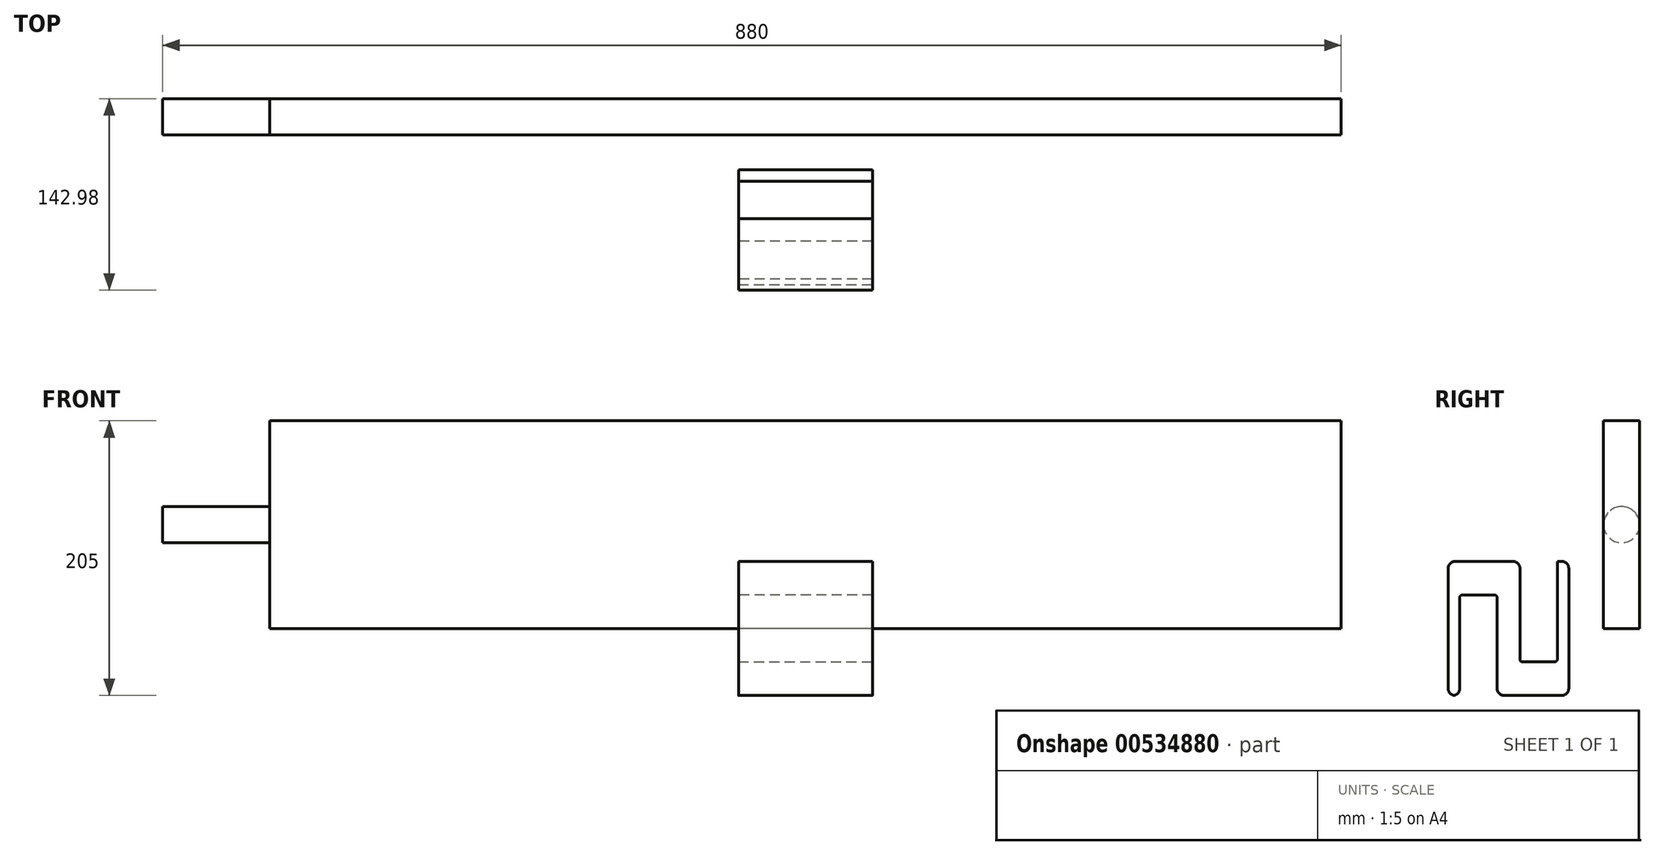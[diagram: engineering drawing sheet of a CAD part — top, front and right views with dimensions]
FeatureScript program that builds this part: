
annotation { "Feature Type Name" : "Feature", "Feature Type Description" : "" }
export const myFeature = defineFeature(function(context is Context, id is Id, definition is map)
    precondition{}
    {
        {
            var Q0;
            Q0=qCreatedBy(makeId("Front.planeOp"),FACE);
            var sketch = newSketch(context, id + "F0", { "sketchPlane" : qUnion([Q0])});
            skLineSegment(sketch, "E0.bottom", {"start": v(50, 50) * mm, "end": v(-50, 50) * mm});
            skLineSegment(sketch, "E0.top", {"start": v(50, -50) * mm, "end": v(-50, -50) * mm});
            skLineSegment(sketch, "E0.left", {"start": v(50, 50) * mm, "end": v(50, -50) * mm});
            skLineSegment(sketch, "E0.right", {"start": v(-50, 50) * mm, "end": v(-50, -50) * mm});
            skPoint(sketch, "E0.middle", {"position": v(0, 0) * mm});
            skSolve(sketch);
        }
        {
            var Q0;
            Q0 = qSketchRegion(id + "F0", true);
            extrude(context, id + "F1", {"entities" : qUnion([Q0]), "endBound" : BoundingType.SYMMETRIC, "depth" : 45 * mm, "offsetDistance" : 25 * mm});
        }
        {
            var Q0;
            Q0=makeQuery(id+"F1.opExtrude","SWEPT_FACE",FACE,{"disambiguationData":[OSD([sQuery(id+"F0.wireOp",EDGE,"E0.left")])]});
            var sketch = newSketch(context, id + "F2", { "sketchPlane" : qUnion([Q0])});
            skLineSegment(sketch, "E1.bottom", {"start": v(-14, 50) * mm, "end": v(14, 50) * mm});
            skLineSegment(sketch, "E1.top", {"start": v(-14, -25) * mm, "end": v(14, -25) * mm});
            skLineSegment(sketch, "E1.left", {"start": v(-14, 50) * mm, "end": v(-14, -25) * mm});
            skLineSegment(sketch, "E1.right", {"start": v(14, 50) * mm, "end": v(14, -25) * mm});
            skLineSegment(sketch, "E2.bottom", {"start": v(14, 50) * mm, "end": v(22, 50) * mm});
            skLineSegment(sketch, "E2.top", {"start": v(14, 100) * mm, "end": v(22, 100) * mm});
            skLineSegment(sketch, "E2.left", {"start": v(14, 50) * mm, "end": v(14, 100) * mm});
            skLineSegment(sketch, "E2.right", {"start": v(22, 50) * mm, "end": v(22, 100) * mm});
            skLineSegment(sketch, "E3.bottom", {"start": v(-14, 50) * mm, "end": v(-22, 50) * mm});
            skLineSegment(sketch, "E3.top", {"start": v(-14, 100) * mm, "end": v(-22, 100) * mm});
            skLineSegment(sketch, "E3.left", {"start": v(-14, 50) * mm, "end": v(-14, 100) * mm});
            skLineSegment(sketch, "E3.right", {"start": v(-22, 50) * mm, "end": v(-22, 100) * mm});
            skSolve(sketch);
        }
        {
            var Q0;
            Q0=makeQuery(id+"F2.imprint","IMPRINT",FACE,{"disambiguationData":[TD([[makeQuery(id+"F2.imprint","IMPRINT",EDGE,{"derivedFrom":sQuery(id+"F2.wireOp",EDGE,"E1.bottom")}),-1.0]])]});
            extrude(context, id + "F3", {"entities" : qUnion([Q0]), "operationType" : NewBodyOperationType.REMOVE, "endBound" : BoundingType.SYMMETRIC, "oppositeDirection" : true, "depth" : 200 * mm, "offsetDistance" : 25 * mm});
        }
        {
            var Q0;
            Q0=qCreatedBy(makeId("Right.planeOp"),FACE);
            var sketch = newSketch(context, id + "F4", { "sketchPlane" : qUnion([Q0])});
            skLineSegment(sketch, "E4.bottom", {"start": v(-22.5, 50) * mm, "end": v(-67.5, 50) * mm});
            skLineSegment(sketch, "E4.top", {"start": v(-22.5, -50) * mm, "end": v(-67.5, -50) * mm});
            skLineSegment(sketch, "E4.left", {"start": v(-22.5, 50) * mm, "end": v(-22.5, -50) * mm});
            skLineSegment(sketch, "E4.right", {"start": v(-67.5, 50) * mm, "end": v(-67.5, -50) * mm});
            skLineSegment(sketch, "E5.bottom", {"start": v(-59, -50) * mm, "end": v(-31, -50) * mm});
            skLineSegment(sketch, "E5.top", {"start": v(-59, 25) * mm, "end": v(-31, 25) * mm});
            skLineSegment(sketch, "E5.left", {"start": v(-59, -50) * mm, "end": v(-59, 25) * mm});
            skLineSegment(sketch, "E5.right", {"start": v(-31, -50) * mm, "end": v(-31, 25) * mm});
            skSolve(sketch);
        }
        {
            var Q0;
            Q0=makeQuery(id+"F4.imprint","IMPRINT",FACE,{"disambiguationData":[TD([[makeQuery(id+"F4.imprint","IMPRINT",EDGE,{"derivedFrom":sQuery(id+"F4.wireOp",EDGE,"E4.bottom")}),1.0]])]});
            extrude(context, id + "F5", {"entities" : qUnion([Q0]), "operationType" : NewBodyOperationType.ADD, "endBound" : BoundingType.SYMMETRIC, "depth" : 100 * mm, "offsetDistance" : 25 * mm});
        }
        {
            var Q0;
            Q0=makeQuery(id+"F3.boolean.opBoolean","COPY",EDGE,{"derivedFrom":makeQuery(id+"F3.opExtrude","SWEPT_EDGE",EDGE,{"disambiguationData":[OSD([sQuery(id+"F0.wireOp",EDGE,"E0.bottom"),sQuery(id+"F0.wireOp",EDGE,"E0.left"),sQuery(id+"F2.wireOp",EDGE,"E1.bottom"),sQuery(id+"F2.wireOp",EDGE,"E1.left")])]})});
            var Q1;
            Q1=makeQuery(id+"F3.boolean.opBoolean","COPY",EDGE,{"derivedFrom":makeQuery(id+"F3.opExtrude","SWEPT_EDGE",EDGE,{"disambiguationData":[OSD([sQuery(id+"F0.wireOp",EDGE,"E0.bottom"),sQuery(id+"F0.wireOp",EDGE,"E0.left"),sQuery(id+"F2.wireOp",EDGE,"E1.bottom"),sQuery(id+"F2.wireOp",EDGE,"E1.right")])]})});
            var Q2;
            Q2=makeQuery(id+"FD36USPxqQOyVSo_1.opExtrude","SWEPT_EDGE",EDGE,{"disambiguationData":[OSD([sQuery(id+"FGtYEwGTLmUSiTy_1.wireOp",EDGE,"bbfad62d-fb5d-4abd-bb75-cb7e10cc127a"),sQuery(id+"FGtYEwGTLmUSiTy_1.wireOp",EDGE,"330299d7-510d-4f56-8d93-4ce1311deff9")])]});
            var Q3;
            Q3=makeQuery(id+"F5.opExtrude","SWEPT_EDGE",EDGE,{"disambiguationData":[OSD([sQuery(id+"F4.wireOp",EDGE,"E4.top"),sQuery(id+"F4.wireOp",EDGE,"E5.bottom"),sQuery(id+"F4.wireOp",EDGE,"E5.left")])]});
            var Q4;
            Q4=makeQuery(id+"F5.opExtrude","SWEPT_EDGE",EDGE,{"disambiguationData":[OSD([sQuery(id+"F4.wireOp",EDGE,"E4.bottom"),sQuery(id+"F4.wireOp",EDGE,"E4.right")])]});
            var Q5;
            Q5=makeQuery(id+"F5.opExtrude","SWEPT_EDGE",EDGE,{"disambiguationData":[OSD([sQuery(id+"F4.wireOp",EDGE,"E4.top"),sQuery(id+"F4.wireOp",EDGE,"E4.right")])]});
            var Q6;
            Q6=makeQuery(id+"F1.opExtrude","CAP_EDGE",EDGE,{"disambiguationData":[OSD([sQuery(id+"F0.wireOp",EDGE,"E0.bottom")])],"isStart":true});
            var Q7;
            Q7=makeQuery(id+"F5.opExtrude","SWEPT_EDGE",EDGE,{"disambiguationData":[OSD([sQuery(id+"F4.wireOp",EDGE,"E4.top"),sQuery(id+"F4.wireOp",EDGE,"E5.bottom"),sQuery(id+"F4.wireOp",EDGE,"E5.right")])]});
            var Q8;
            Q8=makeQuery(id+"F1.opExtrude","CAP_EDGE",EDGE,{"disambiguationData":[OSD([sQuery(id+"F0.wireOp",EDGE,"E0.top")])],"isStart":true});
            fillet(context, id + "F6", {"entities" : qUnion([Q0, Q1, Q2, Q3, Q4, Q5, Q6, Q7, Q8]), "radius" : 5 * mm, "tangentPropagation" : true, "allowEdgeOverflow" : false});
        }
        {
            var Q0;
            Q0=makeQuery(id+"F3.boolean.opBoolean","COPY",EDGE,{"derivedFrom":makeQuery(id+"F3.opExtrude","SWEPT_EDGE",EDGE,{"disambiguationData":[OSD([sQuery(id+"F2.wireOp",EDGE,"E1.top"),sQuery(id+"F2.wireOp",EDGE,"E1.right")])]})});
            var Q1;
            Q1=makeQuery(id+"F3.boolean.opBoolean","COPY",EDGE,{"derivedFrom":makeQuery(id+"F3.opExtrude","SWEPT_EDGE",EDGE,{"disambiguationData":[OSD([sQuery(id+"F2.wireOp",EDGE,"E1.top"),sQuery(id+"F2.wireOp",EDGE,"E1.left")])]})});
            var Q2;
            Q2=makeQuery(id+"F5.opExtrude","SWEPT_EDGE",EDGE,{"disambiguationData":[OSD([sQuery(id+"F4.wireOp",EDGE,"E5.top"),sQuery(id+"F4.wireOp",EDGE,"E5.right")])]});
            var Q3;
            Q3=makeQuery(id+"F5.opExtrude","SWEPT_EDGE",EDGE,{"disambiguationData":[OSD([sQuery(id+"F4.wireOp",EDGE,"E5.top"),sQuery(id+"F4.wireOp",EDGE,"E5.left")])]});
            fillet(context, id + "F7", {"entities" : qUnion([Q0, Q1, Q2, Q3]), "radius" : 2 * mm, "tangentPropagation" : true, "allowEdgeOverflow" : false});
        }
        {
            var Q0;
            Q0=qCreatedBy(makeId("Right.planeOp"),FACE);
            var sketch = newSketch(context, id + "F8", { "sketchPlane" : qUnion([Q0])});
            skLineSegment(sketch, "E6.bottom", {"start": v(48.48, 0) * mm, "end": v(75.48, 0) * mm});
            skLineSegment(sketch, "E6.top", {"start": v(48.48, 155) * mm, "end": v(75.48, 155) * mm});
            skLineSegment(sketch, "E6.left", {"start": v(48.48, 0) * mm, "end": v(48.48, 155) * mm});
            skLineSegment(sketch, "E6.right", {"start": v(75.48, 0) * mm, "end": v(75.48, 155) * mm});
            skSolve(sketch);
        }
        {
            var Q0;
            Q0=makeQuery(id+"F8.imprint","IMPRINT",FACE,{"disambiguationData":[TD([[makeQuery(id+"F8.imprint","IMPRINT",EDGE,{"derivedFrom":sQuery(id+"F8.wireOp",EDGE,"E6.bottom")}),1.0]])]});
            extrude(context, id + "F9", {"entities" : qUnion([Q0]), "endBound" : BoundingType.SYMMETRIC, "depth" : 800 * mm, "offsetDistance" : 25 * mm});
        }
        {
            var Q0;
            Q0=makeQuery(id+"F9.opExtrude","CAP_FACE",FACE,{"disambiguationData":[OSD([sQuery(id+"F8.wireOp",EDGE,"E6.bottom"),sQuery(id+"F8.wireOp",EDGE,"E6.top"),sQuery(id+"F8.wireOp",EDGE,"E6.left"),sQuery(id+"F8.wireOp",EDGE,"E6.right")])],"isStart":true});
            var sketch = newSketch(context, id + "F10", { "sketchPlane" : qUnion([Q0])});
            skCircle(sketch, "E7", {"center": v(-61.98, 77.5) * mm, "radius": 13.5 * mm});
            skPoint(sketch, "E7.centerSnap0", {"position": v(-75.48, 77.5) * mm});
            skSolve(sketch);
        }
        {
            var Q0;
            Q0 = qSketchRegion(id + "F10", true);
            extrude(context, id + "F11", {"entities" : qUnion([Q0]), "operationType" : NewBodyOperationType.ADD, "depth" : 80 * mm, "offsetDistance" : 25 * mm});
        }
    });
